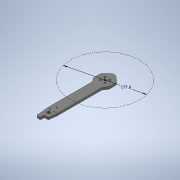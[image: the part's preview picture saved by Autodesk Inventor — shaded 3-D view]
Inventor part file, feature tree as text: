
AUTODESK INVENTOR PART (.ipt)
format: ipt  version: 2020 (Build 240168000, 168)  size: 198,656 bytes
history: native  units: in
note: dims shown in document units (in); Inventor stores cm internally (conversion verified against a paired STEP export)
features: sketch x2, projected_geometry x1
ambient origin geometry x8: Origin, YZ Plane, XZ Plane, XY Plane, X Axis, Y Axis, Z Axis, Center Point
bodies: Solid2 (feature_tree), Solid1 (feature_tree)
feature tree (3):
  sketch  "Sketch1"  dims[d0=7.0in]
  sketch  "Sketch2"  dims[d1=5.72in]
  projected_geometry  "Projected Loop1"
